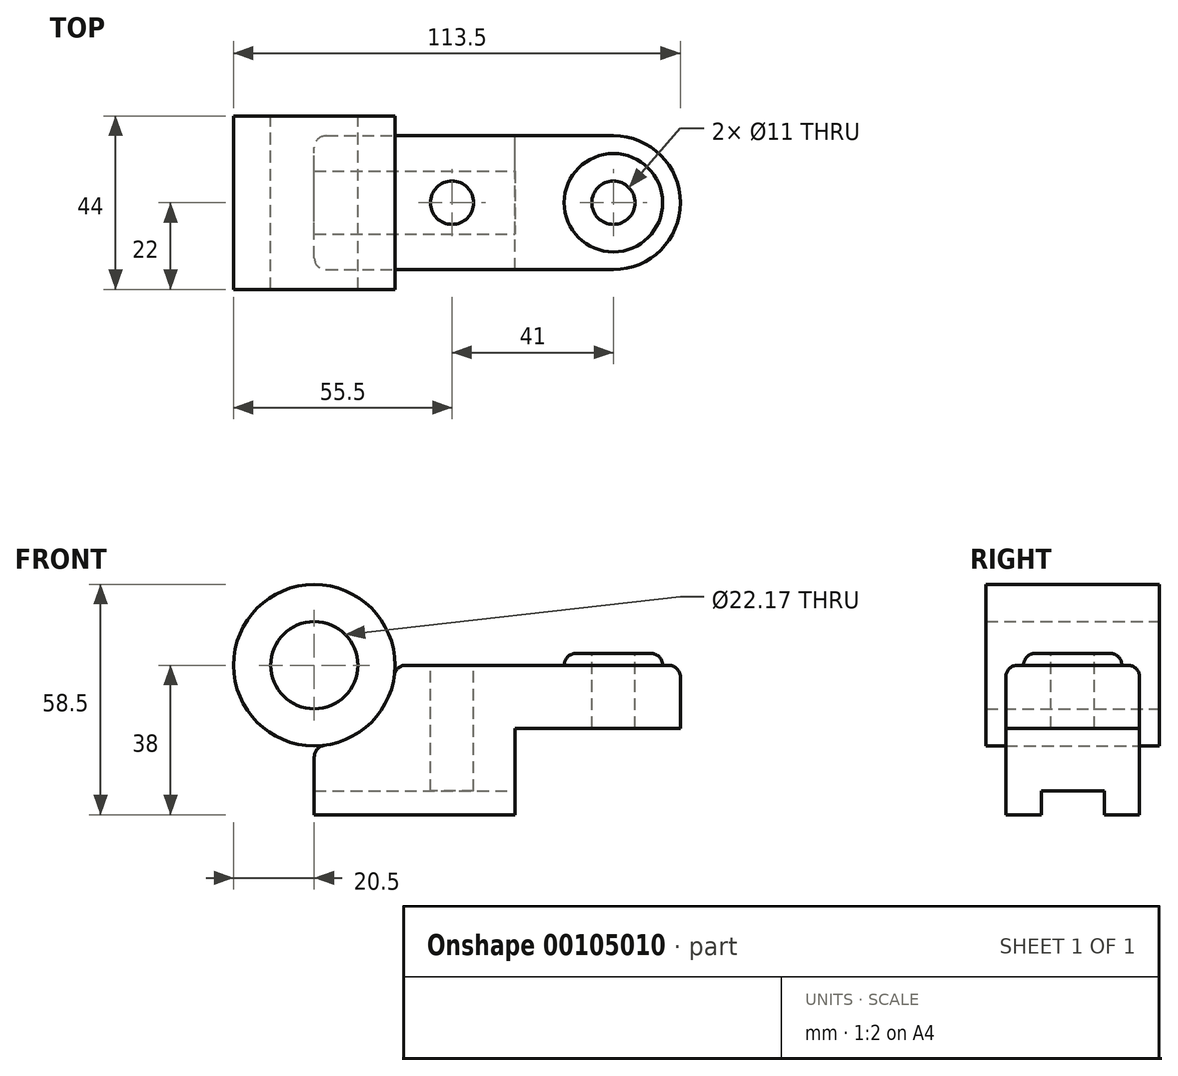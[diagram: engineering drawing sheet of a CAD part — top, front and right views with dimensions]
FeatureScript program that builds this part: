
annotation { "Feature Type Name" : "Feature", "Feature Type Description" : "" }
export const myFeature = defineFeature(function(context is Context, id is Id, definition is map)
    precondition{}
    {
        {
            var Q0;
            Q0=qCreatedBy(makeId("Front.planeOp"),FACE);
            var sketch = newSketch(context, id + "F0", { "sketchPlane" : qUnion([Q0])});
            skLineSegment(sketch, "E0.bottom", {"start": v(0, 0) * mm, "end": v(51, 0) * mm});
            skLineSegment(sketch, "E0.top", {"start": v(0, 38) * mm, "end": v(76, 38) * mm});
            skLineSegment(sketch, "E0.left", {"start": v(0, 0) * mm, "end": v(0, 38) * mm});
            skLineSegment(sketch, "E0.right", {"start": v(76, 22) * mm, "end": v(76, 38) * mm});
            skLineSegment(sketch, "E1.bottom", {"start": v(76, 22) * mm, "end": v(51, 22) * mm});
            skLineSegment(sketch, "E1.right", {"start": v(51, 22) * mm, "end": v(51, 0) * mm});
            skCircle(sketch, "E2", {"center": v(0, 38) * mm, "radius": 11.09 * mm});
            skCircle(sketch, "E3", {"center": v(0, 38) * mm, "radius": 20.5 * mm});
            skSolve(sketch);
        }
        {
            var Q0;
            {var subQ2=sQuery(id+"F0.wireOp",EDGE,"E0.bottom");Q0=makeQuery(id+"F0.imprint","IMPRINT",FACE,{"disambiguationData":[TD([[makeQuery(id+"F0.imprint","IMPRINT",EDGE,{"derivedFrom":subQ2}),1.0]])]});}
            extrude(context, id + "F1", {"entities" : qUnion([Q0]), "endBound" : BoundingType.SYMMETRIC, "depth" : (17 * 2) * mm});
        }
        {
            var Q0;
            {var subQ0=sQuery(id+"F0.wireOp",EDGE,"E3");var subQ1=sQuery(id+"F0.wireOp",EDGE,"E0.top");var subQ2=makeQuery(id+"F0.imprint","INTERSECT",VERTEX,{"derivedFrom":[subQ1,subQ0]});Q0=makeQuery(id+"F0.imprint","IMPRINT",FACE,{"disambiguationData":[TD([[makeQuery(id+"F0.imprint","IMPRINT",EDGE,{"disambiguationData":[TD([[subQ2,1.0]])],"derivedFrom":subQ1}),1.0]])]});}
            var Q1;
            {var subQ0=sQuery(id+"F0.wireOp",EDGE,"E3");var subQ1=sQuery(id+"F0.wireOp",EDGE,"E0.top");var subQ2=makeQuery(id+"F0.imprint","INTERSECT",VERTEX,{"derivedFrom":[subQ1,subQ0]});Q1=makeQuery(id+"F0.imprint","IMPRINT",FACE,{"disambiguationData":[TD([[makeQuery(id+"F0.imprint","IMPRINT",EDGE,{"disambiguationData":[TD([[subQ2,1.0]])],"derivedFrom":subQ1}),-1.0]])]});}
            var Q2;
            Q2=sQuery(id+"F0.wireOp",EDGE,"E3");
            var Q3;
            Q3=sQuery(id+"F0.wireOp",EDGE,"E2");
            extrude(context, id + "F2", {"entities" : qUnion([Q0, Q1]), "surfaceEntities" : qUnion([Q2, Q3]), "endBound" : BoundingType.SYMMETRIC, "depth" : 44 * mm});
        }
        {
            var Q0;
            Q0=makeQuery(id+"F1.opExtrude","SWEPT_FACE",FACE,{"disambiguationData":[OSD([sQuery(id+"F0.wireOp",EDGE,"E0.top")])]});
            var sketch = newSketch(context, id + "F3", { "sketchPlane" : qUnion([Q0])});
            skArc(sketch, "E4", {"start": v(76, -17) * mm, "mid": v(93, 0) * mm, "end": v(76, 17) * mm});
            skSolve(sketch);
        }
        {
            var Q0;
            Q0=makeQuery(id+"F3.imprint","IMPRINT",FACE,{"disambiguationData":[TD([[makeQuery(id+"F3.imprint","IMPRINT",EDGE,{"derivedFrom":sQuery(id+"F3.wireOp",EDGE,"E4")}),1.0]])]});
            var Q1;
            Q1=makeQuery(id+"F1.opExtrude","SWEPT_FACE",FACE,{"disambiguationData":[OSD([sQuery(id+"F0.wireOp",EDGE,"E1.bottom")])]});
            extrude(context, id + "F4", {"entities" : qUnion([Q0]), "operationType" : NewBodyOperationType.ADD, "endBound" : BoundingType.UP_TO_SURFACE, "oppositeDirection" : true, "endBoundEntityFace" : qUnion([Q1]), "depth" : 25 * mm});
        }
        {
            var Q0;
            {var subQ0=sQuery(id+"F0.wireOp",EDGE,"E0.top");Q0=makeQuery(id+"F4.boolean.opBoolean","MERGE",FACE,{"derivedFrom":[makeQuery(id+"F1.opExtrude","SWEPT_FACE",FACE,{"disambiguationData":[OSD([subQ0])]}),makeQuery(id+"F4.opExtrude","CAP_FACE",FACE,{"disambiguationData":[OSD([subQ0,sQuery(id+"F0.wireOp",EDGE,"E0.right"),sQuery(id+"F3.wireOp",EDGE,"E4")])],"isStart":true})]});}
            var sketch = newSketch(context, id + "F5", { "sketchPlane" : qUnion([Q0])});
            skCircle(sketch, "E5", {"center": v(76, 0) * mm, "radius": 12.5 * mm});
            skSolve(sketch);
        }
        {
            var Q0;
            Q0=makeQuery(id+"F5.imprint","IMPRINT",FACE,{"disambiguationData":[TD([[makeQuery(id+"F5.imprint","IMPRINT",EDGE,{"derivedFrom":sQuery(id+"F5.wireOp",EDGE,"E5")}),1.0]])]});
            extrude(context, id + "F6", {"entities" : qUnion([Q0]), "operationType" : NewBodyOperationType.ADD, "depth" : 3 * mm});
        }
        {
            var Q0;
            Q0=makeQuery(id+"F6.opExtrude","CAP_FACE",FACE,{"disambiguationData":[OSD([sQuery(id+"F5.wireOp",EDGE,"E5")])],"isStart":false});
            var sketch = newSketch(context, id + "F7", { "sketchPlane" : qUnion([Q0])});
            skCircle(sketch, "E6", {"center": v(76, 0) * mm, "radius": 5.5 * mm});
            skCircle(sketch, "E7", {"center": v(35, 0) * mm, "radius": 5.5 * mm});
            skSolve(sketch);
        }
        {
            var Q0;
            Q0=makeQuery(id+"F7.imprint","IMPRINT",FACE,{"disambiguationData":[TD([[makeQuery(id+"F7.imprint","IMPRINT",EDGE,{"derivedFrom":sQuery(id+"F7.wireOp",EDGE,"E7")}),1.0]])]});
            var Q1;
            Q1=makeQuery(id+"F7.imprint","IMPRINT",FACE,{"disambiguationData":[TD([[makeQuery(id+"F7.imprint","IMPRINT",EDGE,{"derivedFrom":sQuery(id+"F7.wireOp",EDGE,"E6")}),1.0]])]});
            var Q2;
            Q2=sQuery(id+"F7.wireOp",EDGE,"E7");
            extrude(context, id + "F8", {"entities" : qUnion([Q0, Q1]), "operationType" : NewBodyOperationType.REMOVE, "surfaceEntities" : qUnion([Q2]), "endBound" : BoundingType.THROUGH_ALL, "oppositeDirection" : true, "depth" : 25 * mm});
        }
        {
            var Q0;
            Q0=makeQuery(id+"F1.opExtrude","SWEPT_FACE",FACE,{"disambiguationData":[OSD([sQuery(id+"F0.wireOp",EDGE,"E1.right")])]});
            var sketch = newSketch(context, id + "F9", { "sketchPlane" : qUnion([Q0])});
            skLineSegment(sketch, "E8.bottom", {"start": v(8, 0) * mm, "end": v(-8, 0) * mm});
            skLineSegment(sketch, "E8.top", {"start": v(8, 6) * mm, "end": v(-8, 6) * mm});
            skLineSegment(sketch, "E8.left", {"start": v(8, 0) * mm, "end": v(8, 6) * mm});
            skLineSegment(sketch, "E8.right", {"start": v(-8, 0) * mm, "end": v(-8, 6) * mm});
            skSolve(sketch);
        }
        {
            var Q0;
            Q0=makeQuery(id+"F9.imprint","IMPRINT",FACE,{"disambiguationData":[TD([[makeQuery(id+"F9.imprint","IMPRINT",EDGE,{"derivedFrom":sQuery(id+"F9.wireOp",EDGE,"E8.bottom")}),1.0]])]});
            extrude(context, id + "F10", {"entities" : qUnion([Q0]), "operationType" : NewBodyOperationType.REMOVE, "endBound" : BoundingType.THROUGH_ALL, "oppositeDirection" : true, "depth" : 25 * mm});
        }
        {
            var Q0;
            Q0=makeQuery(id+"F6.opExtrude","CAP_EDGE",EDGE,{"disambiguationData":[OSD([sQuery(id+"F5.wireOp",EDGE,"E5")])],"isStart":false});
            var Q1;
            Q1=makeQuery(id+"F1.opExtrude","SWEPT_EDGE",EDGE,{"disambiguationData":[OSD([sQuery(id+"F0.wireOp",EDGE,"E0.top"),sQuery(id+"F0.wireOp",EDGE,"E3")])]});
            var Q2;
            Q2=makeQuery(id+"F1.opExtrude","CAP_EDGE",EDGE,{"disambiguationData":[OSD([sQuery(id+"F0.wireOp",EDGE,"E3")])],"isStart":false});
            var Q3;
            Q3=makeQuery(id+"F1.opExtrude","CAP_EDGE",EDGE,{"disambiguationData":[OSD([sQuery(id+"F0.wireOp",EDGE,"E3")])],"isStart":true});
            var Q4;
            Q4=makeQuery(id+"F1.opExtrude","SWEPT_EDGE",EDGE,{"disambiguationData":[OSD([sQuery(id+"F0.wireOp",EDGE,"E0.left"),sQuery(id+"F0.wireOp",EDGE,"E3")])]});
            var Q5;
            Q5=makeQuery(id+"F1.opExtrude","CAP_EDGE",EDGE,{"disambiguationData":[OSD([sQuery(id+"F0.wireOp",EDGE,"E0.left")])],"isStart":true});
            var Q6;
            Q6=makeQuery(id+"F1.opExtrude","CAP_EDGE",EDGE,{"disambiguationData":[OSD([sQuery(id+"F0.wireOp",EDGE,"E0.left")])],"isStart":false});
            fillet(context, id + "F11", {"entities" : qUnion([Q0, Q1, Q2, Q3, Q4, Q5, Q6]), "radius" : 3 * mm, "tangentPropagation" : true, "allowEdgeOverflow" : false});
        }
        {
            var Q0;
            Q0=makeQuery(id+"F1.opExtrude","CAP_EDGE",EDGE,{"disambiguationData":[OSD([sQuery(id+"F0.wireOp",EDGE,"E0.top")])],"isStart":false});
            var Q1;
            Q1=makeQuery(id+"F1.opExtrude","CAP_EDGE",EDGE,{"disambiguationData":[OSD([sQuery(id+"F0.wireOp",EDGE,"E0.top")])],"isStart":true});
            fillet(context, id + "F12", {"entities" : qUnion([Q0, Q1]), "radius" : 3 * mm, "tangentPropagation" : true, "allowEdgeOverflow" : false});
        }
    });
